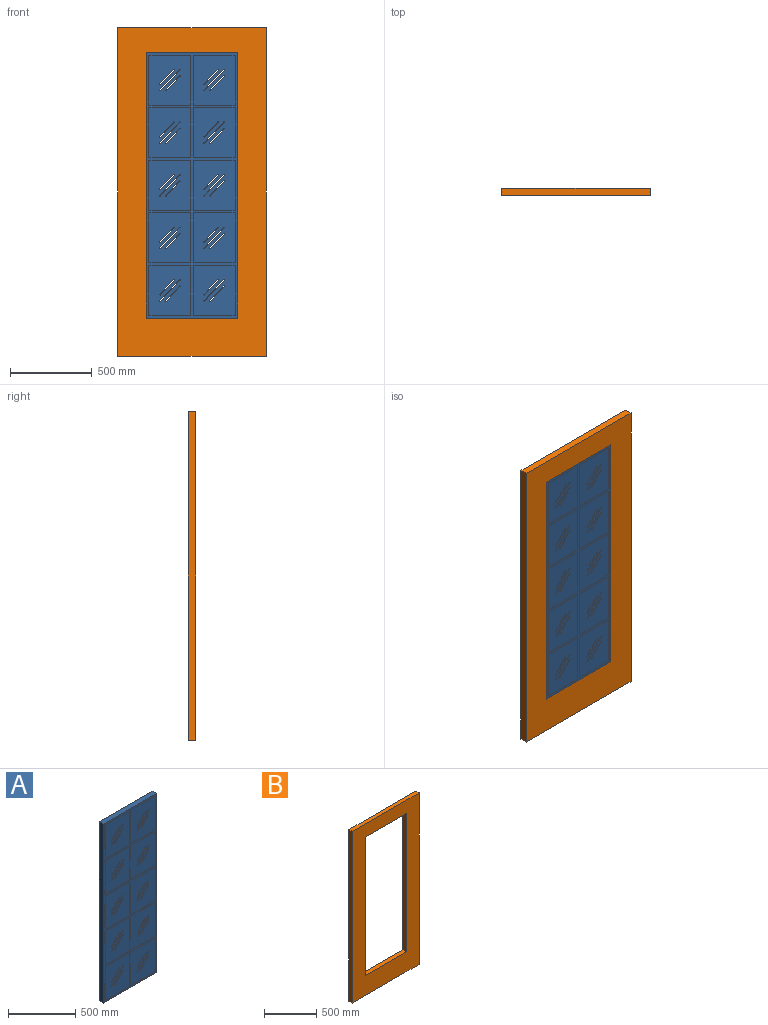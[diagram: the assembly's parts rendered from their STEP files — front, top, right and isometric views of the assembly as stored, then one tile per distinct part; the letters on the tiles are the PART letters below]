
ASSEMBLY  parts=2 mates=1
PART A: 226 faces, bbox 558.8x44.5x1625.6 mm
  f0: plane 306.07x0.64mm, normal (1,0,0), area 194.4mm2, adj f1,f3,f85,f225
  f1: plane 255.59x0.64mm, normal (0,0,-1), area 162.3mm2, adj f0,f2,f85,f225
  f2: plane 306.07x0.64mm, normal (-1,0,0), area 194.4mm2, adj f1,f3,f85,f225
  f3: plane 255.59x0.64mm, normal (0,0,1), area 162.3mm2, adj f0,f2,f85,f225
  f4: plane 306.07x0.64mm, normal (1,0,0), area 194.4mm2, adj f5,f7,f85,f211
  f5: plane 255.59x0.64mm, normal (0,0,-1), area 162.3mm2, adj f4,f6,f85,f211
  f6: plane 306.07x0.64mm, normal (-1,0,0), area 194.4mm2, adj f5,f7,f85,f211
  f7: plane 255.59x0.64mm, normal (0,0,1), area 162.3mm2, adj f4,f6,f85,f211
  f8: plane 255.59x0.64mm, normal (0,0,-1), area 162.3mm2, adj f9,f11,f85,f197
  f9: plane 306.07x0.64mm, normal (-1,0,0), area 194.4mm2, adj f8,f10,f85,f197
  f10: plane 255.59x0.64mm, normal (0,0,1), area 162.3mm2, adj f9,f11,f85,f197
  f11: plane 306.07x0.64mm, normal (1,0,0), area 194.4mm2, adj f8,f10,f85,f197
  f12: plane 306.07x0.64mm, normal (1,0,0), area 194.4mm2, adj f13,f15,f85,f183
  f13: plane 255.59x0.64mm, normal (0,0,-1), area 162.3mm2, adj f12,f14,f85,f183
  f14: plane 306.07x0.64mm, normal (-1,0,0), area 194.4mm2, adj f13,f15,f85,f183
  f15: plane 255.59x0.64mm, normal (0,0,1), area 162.3mm2, adj f12,f14,f85,f183
  f16: plane 306.07x0.64mm, normal (1,0,0), area 194.4mm2, adj f17,f19,f85,f169
  f17: plane 255.59x0.64mm, normal (0,0,-1), area 162.3mm2, adj f16,f18,f85,f169
  f18: plane 306.07x0.64mm, normal (-1,0,0), area 194.4mm2, adj f17,f19,f85,f169
  f19: plane 255.59x0.64mm, normal (0,0,1), area 162.3mm2, adj f16,f18,f85,f169
  f20: plane 255.59x0.64mm, normal (0,0,-1), area 162.3mm2, adj f21,f23,f85,f155
  f21: plane 306.07x0.64mm, normal (-1,0,0), area 194.4mm2, adj f20,f22,f85,f155
  f22: plane 255.59x0.64mm, normal (0,0,1), area 162.3mm2, adj f21,f23,f85,f155
  f23: plane 306.07x0.64mm, normal (1,0,0), area 194.4mm2, adj f20,f22,f85,f155
  f24: plane 255.59x0.64mm, normal (0,0,-1), area 162.3mm2, adj f25,f27,f85,f141
  f25: plane 306.07x0.64mm, normal (-1,0,0), area 194.4mm2, adj f24,f26,f85,f141
  f26: plane 255.59x0.64mm, normal (0,0,1), area 162.3mm2, adj f25,f27,f85,f141
  f27: plane 306.07x0.64mm, normal (1,0,0), area 194.4mm2, adj f24,f26,f85,f141
  f28: plane 306.07x0.64mm, normal (1,0,0), area 194.4mm2, adj f29,f31,f85,f127
  f29: plane 255.59x0.64mm, normal (0,0,-1), area 162.3mm2, adj f28,f30,f85,f127
  f30: plane 306.07x0.64mm, normal (-1,0,0), area 194.4mm2, adj f29,f31,f85,f127
  f31: plane 255.59x0.64mm, normal (0,0,1), area 162.3mm2, adj f28,f30,f85,f127
  f32: plane 306.07x0.64mm, normal (1,0,0), area 194.4mm2, adj f33,f35,f85,f113
  f33: plane 255.59x0.64mm, normal (0,0,-1), area 162.3mm2, adj f32,f34,f85,f113
  f34: plane 306.07x0.64mm, normal (-1,0,0), area 194.4mm2, adj f33,f35,f85,f113
  f35: plane 255.59x0.64mm, normal (0,0,1), area 162.3mm2, adj f32,f34,f85,f113
  f36: plane 255.59x0.64mm, normal (0,0,-1), area 162.3mm2, adj f37,f39,f85,f99
  f37: plane 306.07x0.64mm, normal (-1,0,0), area 194.4mm2, adj f36,f38,f85,f99
  f38: plane 255.59x0.64mm, normal (0,0,1), area 162.3mm2, adj f37,f39,f85,f99
  f39: plane 306.07x0.64mm, normal (1,0,0), area 194.4mm2, adj f36,f38,f85,f99
  f40: plane 306.07x0.64mm, normal (1,0,0), area 194.4mm2, adj f41,f83,f84,f112
  f41: plane 255.59x0.64mm, normal (0,0,-1), area 162.3mm2, adj f40,f42,f84,f112
  f42: plane 306.07x0.64mm, normal (-1,0,0), area 194.4mm2, adj f41,f83,f84,f112
  f43: plane 306.07x0.64mm, normal (1,0,0), area 194.4mm2, adj f44,f73,f84,f126
  f44: plane 255.59x0.64mm, normal (0,0,-1), area 162.3mm2, adj f43,f45,f84,f126
  f45: plane 306.07x0.64mm, normal (-1,0,0), area 194.4mm2, adj f44,f73,f84,f126
  f46: plane 306.07x0.64mm, normal (1,0,0), area 194.4mm2, adj f47,f74,f84,f168
  f47: plane 255.59x0.64mm, normal (0,0,-1), area 162.3mm2, adj f46,f48,f84,f168
  f48: plane 306.07x0.64mm, normal (-1,0,0), area 194.4mm2, adj f47,f74,f84,f168
  f49: plane 306.07x0.64mm, normal (1,0,0), area 194.4mm2, adj f50,f75,f84,f182
  f50: plane 255.59x0.64mm, normal (0,0,-1), area 162.3mm2, adj f49,f51,f84,f182
  f51: plane 306.07x0.64mm, normal (-1,0,0), area 194.4mm2, adj f50,f75,f84,f182
  f52: plane 306.07x0.64mm, normal (1,0,0), area 194.4mm2, adj f53,f76,f84,f224
  f53: plane 255.59x0.64mm, normal (0,0,-1), area 162.3mm2, adj f52,f54,f84,f224
  f54: plane 306.07x0.64mm, normal (-1,0,0), area 194.4mm2, adj f53,f76,f84,f224
  f55: plane 306.07x0.64mm, normal (1,0,0), area 194.4mm2, adj f56,f77,f84,f210
  f56: plane 255.59x0.64mm, normal (0,0,-1), area 162.3mm2, adj f55,f57,f84,f210
  f57: plane 306.07x0.64mm, normal (-1,0,0), area 194.4mm2, adj f56,f77,f84,f210
  f58: plane 558.8x44.45mm, normal (0,0,1), area 24838.7mm2, adj f59,f78,f84,f85
  f59: plane 1625.6x44.45mm, normal (-1,0,0), area 72257.9mm2, adj f58,f60,f84,f85
  f60: plane 558.8x44.45mm, normal (0,0,-1), area 24838.7mm2, adj f59,f78,f84,f85
  f61: plane 255.59x0.64mm, normal (0,0,-1), area 162.3mm2, adj f62,f79,f84,f196
  f62: plane 306.07x0.64mm, normal (-1,0,0), area 194.4mm2, adj f61,f63,f84,f196
  f63: plane 255.59x0.64mm, normal (0,0,1), area 162.3mm2, adj f62,f79,f84,f196
  f64: plane 255.59x0.64mm, normal (0,0,-1), area 162.3mm2, adj f65,f80,f84,f154
  f65: plane 306.07x0.64mm, normal (-1,0,0), area 194.4mm2, adj f64,f66,f84,f154
  f66: plane 255.59x0.64mm, normal (0,0,1), area 162.3mm2, adj f65,f80,f84,f154
  f67: plane 255.59x0.64mm, normal (0,0,-1), area 162.3mm2, adj f68,f81,f84,f140
  f68: plane 306.07x0.64mm, normal (-1,0,0), area 194.4mm2, adj f67,f69,f84,f140
  f69: plane 255.59x0.64mm, normal (0,0,1), area 162.3mm2, adj f68,f81,f84,f140
  f70: plane 255.59x0.64mm, normal (0,0,-1), area 162.3mm2, adj f71,f82,f84,f98
  f71: plane 306.07x0.64mm, normal (-1,0,0), area 194.4mm2, adj f70,f72,f84,f98
  f72: plane 255.59x0.64mm, normal (0,0,1), area 162.3mm2, adj f71,f82,f84,f98
  f73: plane 255.59x0.64mm, normal (0,0,1), area 162.3mm2, adj f43,f45,f84,f126
  f74: plane 255.59x0.64mm, normal (0,0,1), area 162.3mm2, adj f46,f48,f84,f168
  f75: plane 255.59x0.64mm, normal (0,0,1), area 162.3mm2, adj f49,f51,f84,f182
  f76: plane 255.59x0.64mm, normal (0,0,1), area 162.3mm2, adj f52,f54,f84,f224
  f77: plane 255.59x0.64mm, normal (0,0,1), area 162.3mm2, adj f55,f57,f84,f210
  f78: plane 1625.6x44.45mm, normal (1,0,0), area 72257.9mm2, adj f58,f60,f84,f85
  f79: plane 306.07x0.64mm, normal (1,0,0), area 194.4mm2, adj f61,f63,f84,f196
  f80: plane 306.07x0.64mm, normal (1,0,0), area 194.4mm2, adj f64,f66,f84,f154
  f81: plane 306.07x0.64mm, normal (1,0,0), area 194.4mm2, adj f67,f69,f84,f140
  f82: plane 306.07x0.64mm, normal (1,0,0), area 194.4mm2, adj f70,f72,f84,f98
  f83: plane 255.59x0.64mm, normal (0,0,1), area 162.3mm2, adj f40,f42,f84,f112
  f84: plane 1625.6x558.8mm, normal (0,-1,0), area 126108.6mm2, adj f40,f41,f42,f43,f44,f45,f46,f47
  f85: plane 1625.6x558.8mm, normal (0,1,0), area 126108.6mm2, adj f0,f1,f2,f3,f4,f5,f6,f7
  f86: cylinder r=3.17mm len=43.18mm, axis (0,1,0), area 430.7mm2, adj f87,f97,f98,f99
  f87: plane 88.11x82.76mm, normal (-0.73,0,0.68), area 5219.7mm2, adj f86,f88,f98,f99
  f88: cylinder r=3.17mm len=43.18mm, axis (0,1,0), area 430.7mm2, adj f87,f97,f98,f99
  f89: cylinder r=3.17mm len=43.18mm, axis (0,1,0), area 430.7mm2, adj f90,f95,f98,f99
  f90: plane 88.11x82.76mm, normal (-0.73,0,0.68), area 5219.7mm2, adj f89,f91,f98,f99
  f91: cylinder r=3.17mm len=43.18mm, axis (0,1,0), area 430.7mm2, adj f90,f95,f98,f99
  f92: plane 126.21x118.54mm, normal (0.73,0,-0.68), area 7476.7mm2, adj f93,f96,f98,f99
  f93: cylinder r=3.17mm len=43.18mm, axis (0,1,0), area 430.7mm2, adj f92,f94,f98,f99
  f94: plane 126.21x118.54mm, normal (-0.73,0,0.68), area 7476.7mm2, adj f93,f96,f98,f99
  f95: plane 88.11x82.76mm, normal (0.73,0,-0.68), area 5219.7mm2, adj f89,f91,f98,f99
  f96: cylinder r=3.17mm len=43.18mm, axis (0,1,0), area 430.7mm2, adj f92,f94,f98,f99
  f97: plane 88.11x82.76mm, normal (0.73,0,-0.68), area 5219.7mm2, adj f86,f88,f98,f99
  f98: plane 306.07x255.59mm, normal (0,-1,0), area 75497.9mm2, adj f70,f71,f72,f82,f86,f87,f88,f89
  f99: plane 306.07x255.59mm, normal (0,1,0), area 75497.9mm2, adj f36,f37,f38,f39,f86,f87,f88,f89
  f100: cylinder r=3.17mm len=43.18mm, axis (0,1,0), area 430.7mm2, adj f101,f111,f112,f113
  f101: plane 88.11x82.76mm, normal (-0.73,0,0.68), area 5219.7mm2, adj f100,f102,f112,f113
  f102: cylinder r=3.17mm len=43.18mm, axis (0,1,0), area 430.7mm2, adj f101,f111,f112,f113
  f103: cylinder r=3.17mm len=43.18mm, axis (0,1,0), area 430.7mm2, adj f104,f109,f112,f113
  f104: plane 88.11x82.76mm, normal (-0.73,0,0.68), area 5219.7mm2, adj f103,f105,f112,f113
  f105: cylinder r=3.17mm len=43.18mm, axis (0,1,0), area 430.7mm2, adj f104,f109,f112,f113
  f106: plane 126.21x118.54mm, normal (0.73,0,-0.68), area 7476.7mm2, adj f107,f110,f112,f113
  f107: cylinder r=3.17mm len=43.18mm, axis (0,1,0), area 430.7mm2, adj f106,f108,f112,f113
  f108: plane 126.21x118.54mm, normal (-0.73,0,0.68), area 7476.7mm2, adj f107,f110,f112,f113
  f109: plane 88.11x82.76mm, normal (0.73,0,-0.68), area 5219.7mm2, adj f103,f105,f112,f113
  f110: cylinder r=3.17mm len=43.18mm, axis (0,1,0), area 430.7mm2, adj f106,f108,f112,f113
  f111: plane 88.11x82.76mm, normal (0.73,0,-0.68), area 5219.7mm2, adj f100,f102,f112,f113
  f112: plane 306.07x255.59mm, normal (0,-1,0), area 75497.9mm2, adj f40,f41,f42,f83,f100,f101,f102,f103
  f113: plane 306.07x255.59mm, normal (0,1,0), area 75497.9mm2, adj f32,f33,f34,f35,f100,f101,f102,f103
  f114: cylinder r=3.17mm len=43.18mm, axis (0,1,0), area 430.7mm2, adj f115,f125,f126,f127
  f115: plane 88.11x82.76mm, normal (-0.73,0,0.68), area 5219.7mm2, adj f114,f116,f126,f127
  f116: cylinder r=3.17mm len=43.18mm, axis (0,1,0), area 430.7mm2, adj f115,f125,f126,f127
  f117: cylinder r=3.17mm len=43.18mm, axis (0,1,0), area 430.7mm2, adj f118,f123,f126,f127
  f118: plane 88.11x82.76mm, normal (-0.73,0,0.68), area 5219.7mm2, adj f117,f119,f126,f127
  f119: cylinder r=3.17mm len=43.18mm, axis (0,1,0), area 430.7mm2, adj f118,f123,f126,f127
  f120: plane 126.21x118.54mm, normal (0.73,0,-0.68), area 7476.7mm2, adj f121,f124,f126,f127
  f121: cylinder r=3.17mm len=43.18mm, axis (0,1,0), area 430.7mm2, adj f120,f122,f126,f127
  f122: plane 126.21x118.54mm, normal (-0.73,0,0.68), area 7476.7mm2, adj f121,f124,f126,f127
  f123: plane 88.11x82.76mm, normal (0.73,0,-0.68), area 5219.7mm2, adj f117,f119,f126,f127
  f124: cylinder r=3.17mm len=43.18mm, axis (0,1,0), area 430.7mm2, adj f120,f122,f126,f127
  f125: plane 88.11x82.76mm, normal (0.73,0,-0.68), area 5219.7mm2, adj f114,f116,f126,f127
  f126: plane 306.07x255.59mm, normal (0,-1,0), area 75497.9mm2, adj f43,f44,f45,f73,f114,f115,f116,f117
  f127: plane 306.07x255.59mm, normal (0,1,0), area 75497.9mm2, adj f28,f29,f30,f31,f114,f115,f116,f117
  f128: cylinder r=3.17mm len=43.18mm, axis (0,1,0), area 430.7mm2, adj f129,f139,f140,f141
  f129: plane 88.11x82.76mm, normal (-0.73,0,0.68), area 5219.7mm2, adj f128,f130,f140,f141
  f130: cylinder r=3.17mm len=43.18mm, axis (0,1,0), area 430.7mm2, adj f129,f139,f140,f141
  f131: cylinder r=3.17mm len=43.18mm, axis (0,1,0), area 430.7mm2, adj f132,f137,f140,f141
  f132: plane 88.11x82.76mm, normal (-0.73,0,0.68), area 5219.7mm2, adj f131,f133,f140,f141
  f133: cylinder r=3.17mm len=43.18mm, axis (0,1,0), area 430.7mm2, adj f132,f137,f140,f141
  f134: plane 126.21x118.54mm, normal (0.73,0,-0.68), area 7476.7mm2, adj f135,f138,f140,f141
  f135: cylinder r=3.17mm len=43.18mm, axis (0,1,0), area 430.7mm2, adj f134,f136,f140,f141
  f136: plane 126.21x118.54mm, normal (-0.73,0,0.68), area 7476.7mm2, adj f135,f138,f140,f141
  f137: plane 88.11x82.76mm, normal (0.73,0,-0.68), area 5219.7mm2, adj f131,f133,f140,f141
  f138: cylinder r=3.17mm len=43.18mm, axis (0,1,0), area 430.7mm2, adj f134,f136,f140,f141
  f139: plane 88.11x82.76mm, normal (0.73,0,-0.68), area 5219.7mm2, adj f128,f130,f140,f141
  f140: plane 306.07x255.59mm, normal (0,-1,0), area 75497.9mm2, adj f67,f68,f69,f81,f128,f129,f130,f131
  f141: plane 306.07x255.59mm, normal (0,1,0), area 75497.9mm2, adj f24,f25,f26,f27,f128,f129,f130,f131
  f142: cylinder r=3.17mm len=43.18mm, axis (0,1,0), area 430.7mm2, adj f143,f153,f154,f155
  f143: plane 88.11x82.76mm, normal (-0.73,0,0.68), area 5219.7mm2, adj f142,f144,f154,f155
  f144: cylinder r=3.17mm len=43.18mm, axis (0,1,0), area 430.7mm2, adj f143,f153,f154,f155
  f145: cylinder r=3.17mm len=43.18mm, axis (0,1,0), area 430.7mm2, adj f146,f151,f154,f155
  f146: plane 88.11x82.76mm, normal (-0.73,0,0.68), area 5219.7mm2, adj f145,f147,f154,f155
  f147: cylinder r=3.17mm len=43.18mm, axis (0,1,0), area 430.7mm2, adj f146,f151,f154,f155
  f148: plane 126.21x118.54mm, normal (0.73,0,-0.68), area 7476.7mm2, adj f149,f152,f154,f155
  f149: cylinder r=3.17mm len=43.18mm, axis (0,1,0), area 430.7mm2, adj f148,f150,f154,f155
  f150: plane 126.21x118.54mm, normal (-0.73,0,0.68), area 7476.7mm2, adj f149,f152,f154,f155
  f151: plane 88.11x82.76mm, normal (0.73,0,-0.68), area 5219.7mm2, adj f145,f147,f154,f155
  f152: cylinder r=3.17mm len=43.18mm, axis (0,1,0), area 430.7mm2, adj f148,f150,f154,f155
  f153: plane 88.11x82.76mm, normal (0.73,0,-0.68), area 5219.7mm2, adj f142,f144,f154,f155
  f154: plane 306.07x255.59mm, normal (0,-1,0), area 75497.9mm2, adj f64,f65,f66,f80,f142,f143,f144,f145
  f155: plane 306.07x255.59mm, normal (0,1,0), area 75497.9mm2, adj f20,f21,f22,f23,f142,f143,f144,f145
  f156: cylinder r=3.17mm len=43.18mm, axis (0,1,0), area 430.7mm2, adj f157,f167,f168,f169
  f157: plane 88.11x82.76mm, normal (-0.73,0,0.68), area 5219.7mm2, adj f156,f158,f168,f169
  f158: cylinder r=3.17mm len=43.18mm, axis (0,1,0), area 430.7mm2, adj f157,f167,f168,f169
  f159: cylinder r=3.17mm len=43.18mm, axis (0,1,0), area 430.7mm2, adj f160,f165,f168,f169
  f160: plane 88.11x82.76mm, normal (-0.73,0,0.68), area 5219.7mm2, adj f159,f161,f168,f169
  f161: cylinder r=3.17mm len=43.18mm, axis (0,1,0), area 430.7mm2, adj f160,f165,f168,f169
  f162: plane 126.21x118.54mm, normal (0.73,0,-0.68), area 7476.7mm2, adj f163,f166,f168,f169
  f163: cylinder r=3.17mm len=43.18mm, axis (0,1,0), area 430.7mm2, adj f162,f164,f168,f169
  f164: plane 126.21x118.54mm, normal (-0.73,0,0.68), area 7476.7mm2, adj f163,f166,f168,f169
  f165: plane 88.11x82.76mm, normal (0.73,0,-0.68), area 5219.7mm2, adj f159,f161,f168,f169
  f166: cylinder r=3.17mm len=43.18mm, axis (0,1,0), area 430.7mm2, adj f162,f164,f168,f169
  f167: plane 88.11x82.76mm, normal (0.73,0,-0.68), area 5219.7mm2, adj f156,f158,f168,f169
  f168: plane 306.07x255.59mm, normal (0,-1,0), area 75497.9mm2, adj f46,f47,f48,f74,f156,f157,f158,f159
  f169: plane 306.07x255.59mm, normal (0,1,0), area 75497.9mm2, adj f16,f17,f18,f19,f156,f157,f158,f159
  f170: cylinder r=3.17mm len=43.18mm, axis (0,1,0), area 430.7mm2, adj f171,f181,f182,f183
  f171: plane 88.11x82.76mm, normal (-0.73,0,0.68), area 5219.7mm2, adj f170,f172,f182,f183
  f172: cylinder r=3.17mm len=43.18mm, axis (0,1,0), area 430.7mm2, adj f171,f181,f182,f183
  f173: cylinder r=3.17mm len=43.18mm, axis (0,1,0), area 430.7mm2, adj f174,f179,f182,f183
  f174: plane 88.11x82.76mm, normal (-0.73,0,0.68), area 5219.7mm2, adj f173,f175,f182,f183
  f175: cylinder r=3.17mm len=43.18mm, axis (0,1,0), area 430.7mm2, adj f174,f179,f182,f183
  f176: plane 126.21x118.54mm, normal (0.73,0,-0.68), area 7476.7mm2, adj f177,f180,f182,f183
  f177: cylinder r=3.17mm len=43.18mm, axis (0,1,0), area 430.7mm2, adj f176,f178,f182,f183
  f178: plane 126.21x118.54mm, normal (-0.73,0,0.68), area 7476.7mm2, adj f177,f180,f182,f183
  f179: plane 88.11x82.76mm, normal (0.73,0,-0.68), area 5219.7mm2, adj f173,f175,f182,f183
  f180: cylinder r=3.17mm len=43.18mm, axis (0,1,0), area 430.7mm2, adj f176,f178,f182,f183
  f181: plane 88.11x82.76mm, normal (0.73,0,-0.68), area 5219.7mm2, adj f170,f172,f182,f183
  f182: plane 306.07x255.59mm, normal (0,-1,0), area 75497.9mm2, adj f49,f50,f51,f75,f170,f171,f172,f173
  f183: plane 306.07x255.59mm, normal (0,1,0), area 75497.9mm2, adj f12,f13,f14,f15,f170,f171,f172,f173
  f184: cylinder r=3.17mm len=43.18mm, axis (0,1,0), area 430.7mm2, adj f185,f195,f196,f197
  f185: plane 88.11x82.76mm, normal (-0.73,0,0.68), area 5219.7mm2, adj f184,f186,f196,f197
  f186: cylinder r=3.17mm len=43.18mm, axis (0,1,0), area 430.7mm2, adj f185,f195,f196,f197
  f187: cylinder r=3.17mm len=43.18mm, axis (0,1,0), area 430.7mm2, adj f188,f193,f196,f197
  f188: plane 88.11x82.76mm, normal (-0.73,0,0.68), area 5219.7mm2, adj f187,f189,f196,f197
  f189: cylinder r=3.17mm len=43.18mm, axis (0,1,0), area 430.7mm2, adj f188,f193,f196,f197
  f190: plane 126.21x118.54mm, normal (0.73,0,-0.68), area 7476.7mm2, adj f191,f194,f196,f197
  f191: cylinder r=3.17mm len=43.18mm, axis (0,1,0), area 430.7mm2, adj f190,f192,f196,f197
  f192: plane 126.21x118.54mm, normal (-0.73,0,0.68), area 7476.7mm2, adj f191,f194,f196,f197
  f193: plane 88.11x82.76mm, normal (0.73,0,-0.68), area 5219.7mm2, adj f187,f189,f196,f197
  f194: cylinder r=3.17mm len=43.18mm, axis (0,1,0), area 430.7mm2, adj f190,f192,f196,f197
  f195: plane 88.11x82.76mm, normal (0.73,0,-0.68), area 5219.7mm2, adj f184,f186,f196,f197
  f196: plane 306.07x255.59mm, normal (0,-1,0), area 75497.9mm2, adj f61,f62,f63,f79,f184,f185,f186,f187
  f197: plane 306.07x255.59mm, normal (0,1,0), area 75497.9mm2, adj f8,f9,f10,f11,f184,f185,f186,f187
  f198: plane 88.11x82.76mm, normal (-0.73,0,0.68), area 5219.7mm2, adj f199,f209,f210,f211
  f199: cylinder r=3.17mm len=43.18mm, axis (0,1,0), area 430.7mm2, adj f198,f200,f210,f211
  f200: plane 88.11x82.76mm, normal (0.73,0,-0.68), area 5219.7mm2, adj f199,f209,f210,f211
  f201: plane 88.11x82.76mm, normal (-0.73,0,0.68), area 5219.7mm2, adj f202,f207,f210,f211
  f202: cylinder r=3.17mm len=43.18mm, axis (0,1,0), area 430.7mm2, adj f201,f203,f210,f211
  f203: plane 88.11x82.76mm, normal (0.73,0,-0.68), area 5219.7mm2, adj f202,f207,f210,f211
  f204: plane 126.21x118.54mm, normal (-0.73,0,0.68), area 7476.7mm2, adj f205,f208,f210,f211
  f205: cylinder r=3.17mm len=43.18mm, axis (0,1,0), area 430.7mm2, adj f204,f206,f210,f211
  f206: plane 126.21x118.54mm, normal (0.73,0,-0.68), area 7476.7mm2, adj f205,f208,f210,f211
  f207: cylinder r=3.17mm len=43.18mm, axis (0,1,0), area 430.7mm2, adj f201,f203,f210,f211
  f208: cylinder r=3.17mm len=43.18mm, axis (0,1,0), area 430.7mm2, adj f204,f206,f210,f211
  f209: cylinder r=3.17mm len=43.18mm, axis (0,1,0), area 430.7mm2, adj f198,f200,f210,f211
  f210: plane 306.07x255.59mm, normal (0,-1,0), area 75497.9mm2, adj f55,f56,f57,f77,f198,f199,f200,f201
  f211: plane 306.07x255.59mm, normal (0,1,0), area 75497.9mm2, adj f4,f5,f6,f7,f198,f199,f200,f201
  f212: cylinder r=3.17mm len=43.18mm, axis (0,1,0), area 430.7mm2, adj f213,f223,f224,f225
  f213: plane 88.11x82.76mm, normal (-0.73,0,0.68), area 5219.7mm2, adj f212,f214,f224,f225
  f214: cylinder r=3.17mm len=43.18mm, axis (0,1,0), area 430.7mm2, adj f213,f223,f224,f225
  f215: cylinder r=3.17mm len=43.18mm, axis (0,1,0), area 430.7mm2, adj f216,f221,f224,f225
  f216: plane 88.11x82.76mm, normal (-0.73,0,0.68), area 5219.7mm2, adj f215,f217,f224,f225
  f217: cylinder r=3.17mm len=43.18mm, axis (0,1,0), area 430.7mm2, adj f216,f221,f224,f225
  f218: plane 126.21x118.54mm, normal (0.73,0,-0.68), area 7476.7mm2, adj f219,f222,f224,f225
  f219: cylinder r=3.17mm len=43.18mm, axis (0,1,0), area 430.7mm2, adj f218,f220,f224,f225
  f220: plane 126.21x118.54mm, normal (-0.73,0,0.68), area 7476.7mm2, adj f219,f222,f224,f225
  f221: plane 88.11x82.76mm, normal (0.73,0,-0.68), area 5219.7mm2, adj f215,f217,f224,f225
  f222: cylinder r=3.17mm len=43.18mm, axis (0,1,0), area 430.7mm2, adj f218,f220,f224,f225
  f223: plane 88.11x82.76mm, normal (0.73,0,-0.68), area 5219.7mm2, adj f212,f214,f224,f225
  f224: plane 306.07x255.59mm, normal (0,-1,0), area 75497.9mm2, adj f52,f53,f54,f76,f212,f213,f214,f215
  f225: plane 306.07x255.59mm, normal (0,1,0), area 75497.9mm2, adj f0,f1,f2,f3,f212,f213,f214,f215
PART B: 10 faces, bbox 908.1x44.5x2013 mm
  f0: plane 908.05x44.45mm, normal (0,0,1), area 40362.8mm2, adj f1,f7,f8,f9
  f1: plane 2012.95x44.45mm, normal (-1,0,0), area 89475.6mm2, adj f0,f2,f8,f9
  f2: plane 908.05x44.45mm, normal (0,0,-1), area 40362.8mm2, adj f1,f7,f8,f9
  f3: plane 558.8x44.45mm, normal (0,0,1), area 24838.7mm2, adj f4,f6,f8,f9
  f4: plane 1625.6x44.45mm, normal (1,0,0), area 72257.9mm2, adj f3,f5,f8,f9
  f5: plane 558.8x44.45mm, normal (0,0,-1), area 24838.7mm2, adj f4,f6,f8,f9
  f6: plane 1625.6x44.45mm, normal (-1,0,0), area 72257.9mm2, adj f3,f5,f8,f9
  f7: plane 2012.95x44.45mm, normal (1,0,0), area 89475.6mm2, adj f0,f2,f8,f9
  f8: plane 2012.95x908.05mm, normal (0,-1,0), area 919474mm2, adj f0,f1,f2,f3,f4,f5,f6,f7
  f9: plane 2012.95x908.05mm, normal (0,1,0), area 919474mm2, adj f0,f1,f2,f3,f4,f5,f6,f7
PLACE A t=(-121.84,578.13,-53.05)mm
PLACE B t=(-296.46,578.13,-288)mm fixed
MATE fastened A.f58 <-> B.f5  axis (0,0,1) through (157.56,578.13,1572.55)mm
